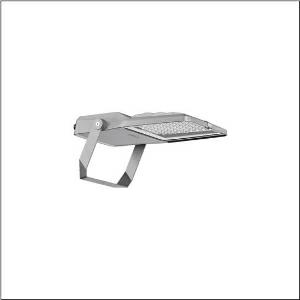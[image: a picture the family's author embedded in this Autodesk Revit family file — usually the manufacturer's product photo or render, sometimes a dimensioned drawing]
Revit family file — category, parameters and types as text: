
# Revit family: floodlight_fl_21_iq_mini___pl61_5xa7772c5c1a_22e4
name_source: partatom
category: Lighting Fixtures
units: mm (PartAtom-declared; Revit-internal decimal feet)

## family parameters
Cut with Voids When Loaded = No
Host = Face
Light Source = No
Part Type = Normal
Room Calculation Point = No
Round Connector Dimension = Use Diameter
Shared = No

## types (1)
- --- (1 x LED, 11180 lm, 87.2 W, 4000K)
    Apparent Load = 87 VA
    CIE Flux Codes = 33 65 98 100 100
    Color Rendering = 80
    Color Temperature = 4000K
    Default Elevation = 1800 mm
    Description = Floodlight FL 21 iQ mini, floodlight, primary light control with lens, of PMMA, primary optical cover: protective disc, of toughened safety glass, transparent, light distribution: PL61, light emission: direct distribution, installation type: surface-mounted, LED, High Power LED, rated luminous flux: 11.180lm, luminous efficacy: 128lm/W, light colour: 840, colour temperature: 4000K, control gear: iQ Street-Remote/DALI, control: Street-Remote, Auto-Match, Temp-Guard, Night-Set, Smart-Wire, Desk-Remote (wireless, voltage-free reading and setting of iQ features in the workshop via application-optimized NFC function/RFID function), optimised constant luminous flux control (CLO 2.0), with terminal, 6-pole, mains connection: 220..240V, AC, 50/60Hz, start of lifetime: 87W, end of service life: 92W, reduction: 40W, luminaire housing, of diecast aluminium, powder-coated, Siteco® metallic grey (DB 702S), corrosivity category C5 mid according to DIN EN ISO 12944, suitable for swimming pools, chlorine-resistant, sealing non-destructively replaceable, mounting bracket, of steel, galvanised, powder-coated, Siteco® metallic grey (DB 702S), protection rating (complete): IP66, insulation class (complete): insulation class II (safety insulation), certification: CE, ENEC, VDE, protection symbol: D, impact resistance: IK08, permissible operating ambient temperature: -40..+40°C, permissible operating ambient temperature for outdoor applications: -40..+50°C, standard: DIN EN 12944, LABS conformity tested according to VDMA 24364:2018-05, packaging unit: 1 piece

Light Distribution: PL61
    Height = 70 mm
    Lamp = 1 x LED
    Lamp Light Flux = 11180 lm
    Lamp Power = 87.2 W
    Lamp count = 1
    Length = 485 mm
    Luminous efficacy = 128 lm/W
    Manufacturer = Siteco
    ModVariant = No
    Model = 5XA7772C5C1A
    Number of Poles = 1
    OnlyDefault = Yes
    Power Factor = 1
    Product Name = Floodlight FL 21 iQ mini | PL61
    Product group = floodlight | pylon annexe
    ProductGroupID = 6200
    Protection Class = Protection class II
    Protection Degree = IP 66
    RLX_Detail_Level = 1
    RLX_Emergency_Light_Flux = 0 lm
    RLX_Emergency_Type = 0
    RLX_Emergency_Type_DB = No
    RlxData = <blob elided: 96413 chars, md5=bebb8270>
    Socket = socket
    Standby Power = 0 W
    System Light Flux = 11180 lm
    System Power = 87 W
    Type Comments = factory setting: luminous flux: 100 % | dim-lin: 254 | 456 mA
    Type Image = l_1006845.jpg
    URL = http://relux.com
    VarID = @adj_172864
    Voltage = 0 V
    Weight = 0.00 kg
    Width = 337 mm

## geometry (parser evidence)
native form markers: Blend x4, Sweep x13
no freeform markers — native parametric forms only
